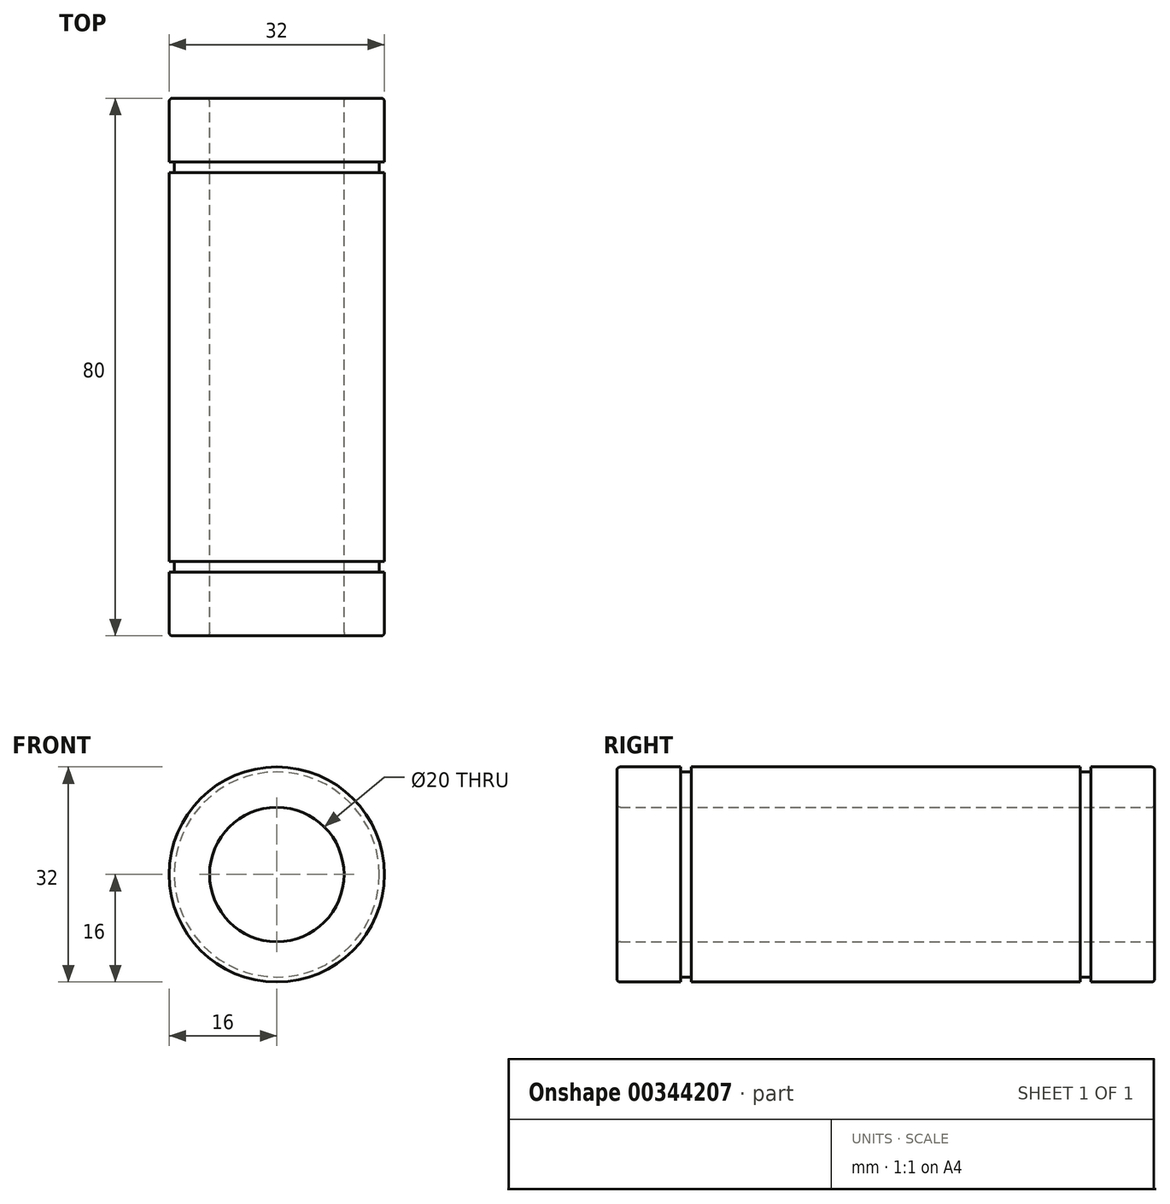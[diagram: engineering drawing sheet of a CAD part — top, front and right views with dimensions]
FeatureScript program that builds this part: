
annotation { "Feature Type Name" : "Feature", "Feature Type Description" : "" }
export const myFeature = defineFeature(function(context is Context, id is Id, definition is map)
    precondition{}
    {
        {
            var Q0;
            Q0=qCreatedBy(makeId("Top.planeOp"),FACE);
            var sketch = newSketch(context, id + "F0", { "sketchPlane" : qUnion([Q0])});
            skLineSegment(sketch, "E0", {"start": v(10, 0) * mm, "end": v(10, -80) * mm});
            skLineSegment(sketch, "E1", {"start": v(10, -80) * mm, "end": v(16, -80) * mm});
            skLineSegment(sketch, "E2", {"start": v(16, -80) * mm, "end": v(16, -70.5) * mm});
            skLineSegment(sketch, "E3", {"start": v(16, 0) * mm, "end": v(10, 0) * mm});
            skLineSegment(sketch, "E4.bottom", {"start": v(15.25, -9.5) * mm, "end": v(16, -9.5) * mm});
            skLineSegment(sketch, "E4.top", {"start": v(15.25, -11.1) * mm, "end": v(16, -11.1) * mm});
            skLineSegment(sketch, "E4.left", {"start": v(15.25, -9.5) * mm, "end": v(15.25, -11.1) * mm});
            skLineSegment(sketch, "E5.bottom", {"start": v(15.25, -68.9) * mm, "end": v(16, -68.9) * mm});
            skLineSegment(sketch, "E5.top", {"start": v(15.25, -70.5) * mm, "end": v(16, -70.5) * mm});
            skLineSegment(sketch, "E5.left", {"start": v(15.25, -68.9) * mm, "end": v(15.25, -70.5) * mm});
            skLineSegment(sketch, "E6.trimOffspring", {"start": v(16, -9.5) * mm, "end": v(16, 0) * mm});
            skLineSegment(sketch, "E7.trimOffspring", {"start": v(16, -68.9) * mm, "end": v(16, -11.1) * mm});
            skLineSegment(sketch, "E8", {"start": v(0, 0) * mm, "end": v(0, -57.53) * mm, "construction": true});
            skSolve(sketch);
        }
        {
            var Q0;
            Q0 = qSketchRegion(id + "F0", true);
            var Q1;
            Q1=sQuery(id+"F0.wireOp",EDGE,"E8");
            revolve(context, id + "F1", {"entities" : qUnion([Q0]), "axis" : qUnion([Q1]), "revolveType" : RevolveType.FULL});
        }
        {
            var Q0;
            Q0=makeQuery(id+"F1.opRevolve","SWEPT_FACE",FACE,{"disambiguationData":[OSD([sQuery(id+"F0.wireOp",EDGE,"E1")])]});
            var Q1;
            Q1=makeQuery(id+"F1.opRevolve","SWEPT_FACE",FACE,{"disambiguationData":[OSD([sQuery(id+"F0.wireOp",EDGE,"E3")])]});
            fillet(context, id + "F2", {"entities" : qUnion([Q0, Q1]), "radius" : .5 * mm, "tangentPropagation" : true, "allowEdgeOverflow" : false});
        }
    });
